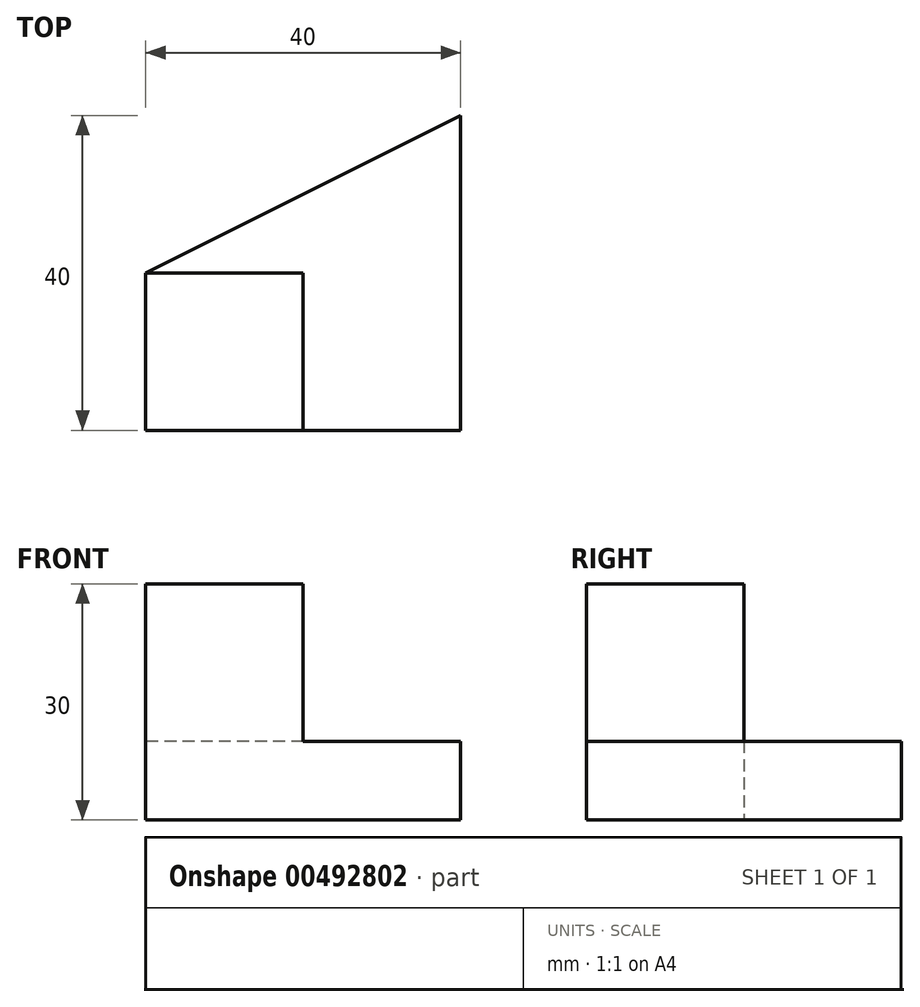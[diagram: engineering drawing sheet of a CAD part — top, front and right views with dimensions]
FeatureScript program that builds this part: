
annotation { "Feature Type Name" : "Feature", "Feature Type Description" : "" }
export const myFeature = defineFeature(function(context is Context, id is Id, definition is map)
    precondition{}
    {
        {
            var Q0;
            Q0=qCreatedBy(makeId("Top.planeOp"),FACE);
            var sketch = newSketch(context, id + "F0", { "sketchPlane" : qUnion([Q0])});
            skLineSegment(sketch, "E0", {"start": v(0, 0) * mm, "end": v(0, -20) * mm});
            skLineSegment(sketch, "E1", {"start": v(0, -20) * mm, "end": v(40, -20) * mm});
            skLineSegment(sketch, "E2", {"start": v(40, -20) * mm, "end": v(40, 20) * mm});
            skLineSegment(sketch, "E3", {"start": v(40, 20) * mm, "end": v(0, 0) * mm});
            skSolve(sketch);
        }
        {
            var Q0;
            Q0=qCreatedBy(makeId("Top.planeOp"),FACE);
            var sketch = newSketch(context, id + "F1", { "sketchPlane" : qUnion([Q0])});
            skLineSegment(sketch, "E4", {"start": v(0, 0) * mm, "end": v(20, 0) * mm});
            skLineSegment(sketch, "E5", {"start": v(20, 0) * mm, "end": v(20, -20) * mm});
            skLineSegment(sketch, "E6", {"start": v(20, -20) * mm, "end": v(0, -20) * mm});
            skLineSegment(sketch, "E7", {"start": v(0, -20) * mm, "end": v(0, 0) * mm});
            skSolve(sketch);
        }
        {
            var Q0;
            Q0 = qSketchRegion(id + "F0", true);
            extrude(context, id + "F2", {"entities" : qUnion([Q0]), "depth" : 10 * mm});
        }
        {
            var Q0;
            Q0 = qSketchRegion(id + "F1", true);
            extrude(context, id + "F3", {"entities" : qUnion([Q0]), "operationType" : NewBodyOperationType.ADD, "depth" : 30 * mm});
        }
    });
